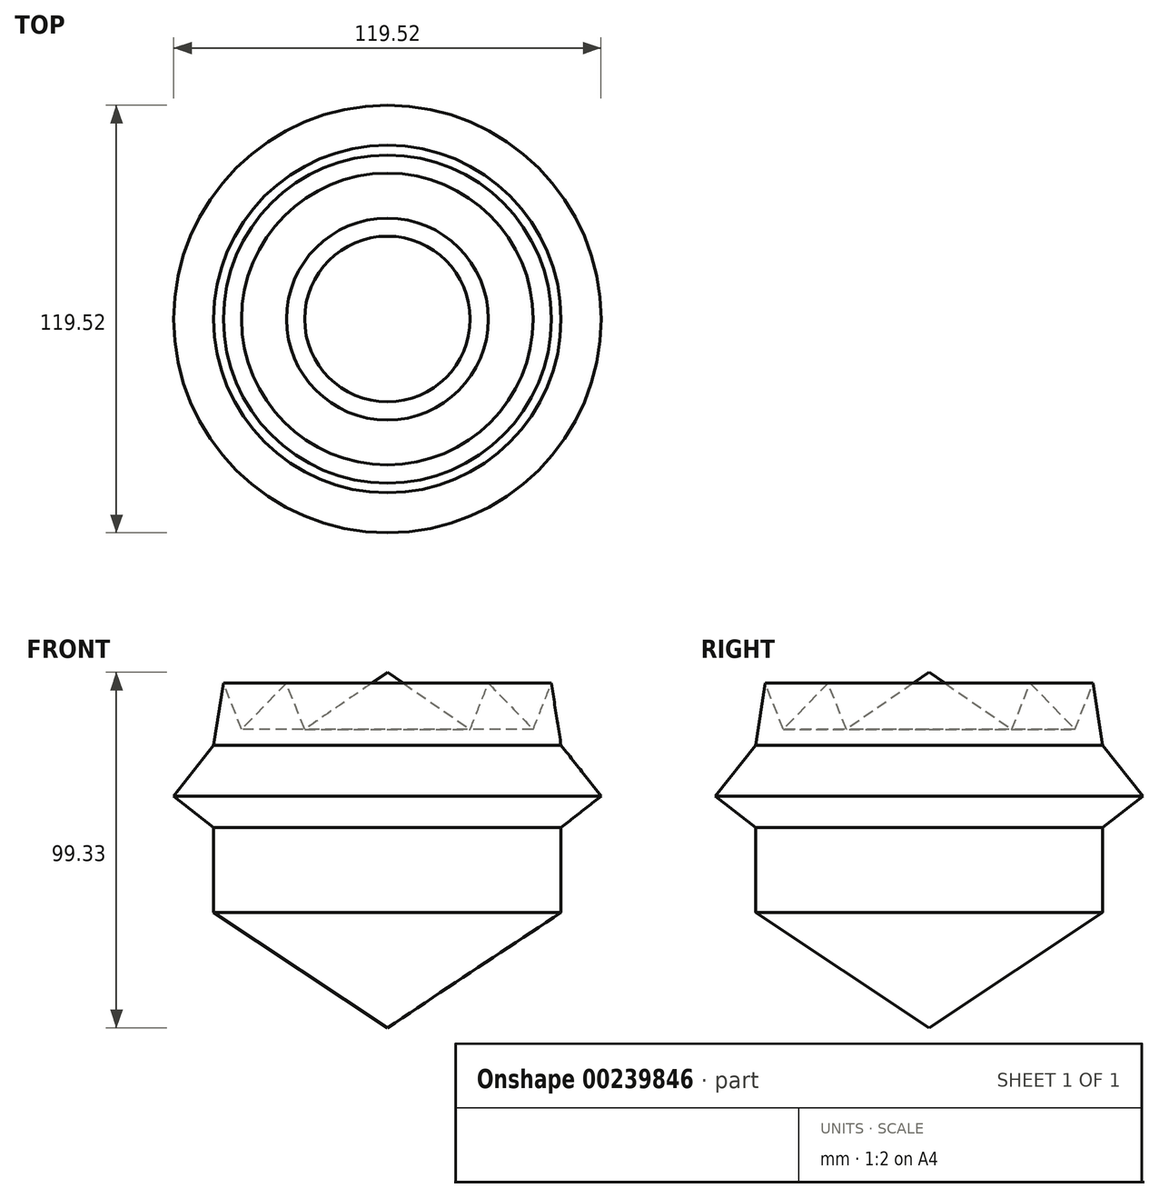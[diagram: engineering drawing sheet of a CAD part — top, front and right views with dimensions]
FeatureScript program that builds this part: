
annotation { "Feature Type Name" : "Feature", "Feature Type Description" : "" }
export const myFeature = defineFeature(function(context is Context, id is Id, definition is map)
    precondition{}
    {
        {
            var Q0;
            Q0=qCreatedBy(makeId("Front.planeOp"),FACE);
            var sketch = newSketch(context, id + "F0", { "sketchPlane" : qUnion([Q0])});
            skLineSegment(sketch, "E0", {"start": v(0, -45.9) * mm, "end": v(-48.57, -13.7) * mm});
            skLineSegment(sketch, "E1", {"start": v(-48.57, -13.7) * mm, "end": v(-48.57, 10.04) * mm});
            skLineSegment(sketch, "E2", {"start": v(-48.57, 10.04) * mm, "end": v(-59.76, 18.85) * mm});
            skLineSegment(sketch, "E3", {"start": v(-59.76, 18.85) * mm, "end": v(-48.57, 33.05) * mm});
            skLineSegment(sketch, "E4", {"start": v(-48.57, 33.05) * mm, "end": v(-45.86, 50.38) * mm});
            skLineSegment(sketch, "E5", {"start": v(-45.86, 50.38) * mm, "end": v(-40.78, 37.5) * mm});
            skLineSegment(sketch, "E6", {"start": v(-40.78, 37.5) * mm, "end": v(-28.23, 50.38) * mm});
            skLineSegment(sketch, "E7", {"start": v(-28.23, 50.38) * mm, "end": v(-23.15, 37.5) * mm});
            skLineSegment(sketch, "E8", {"start": v(-23.15, 37.5) * mm, "end": v(0, 53.43) * mm});
            skLineSegment(sketch, "E9", {"start": v(0, 53.43) * mm, "end": v(0, -45.9) * mm});
            skSolve(sketch);
        }
        {
            var Q0;
            Q0=makeQuery(id+"F0.imprint","IMPRINT",FACE,{"disambiguationData":[TD([[makeQuery(id+"F0.imprint","IMPRINT",EDGE,{"derivedFrom":sQuery(id+"F0.wireOp",EDGE,"E0")}),-1.0]])]});
            var Q1;
            Q1=sQuery(id+"F0.wireOp",EDGE,"E9");
            revolve(context, id + "F1", {"entities" : qUnion([Q0]), "axis" : qUnion([Q1]), "revolveType" : RevolveType.FULL});
        }
    });
